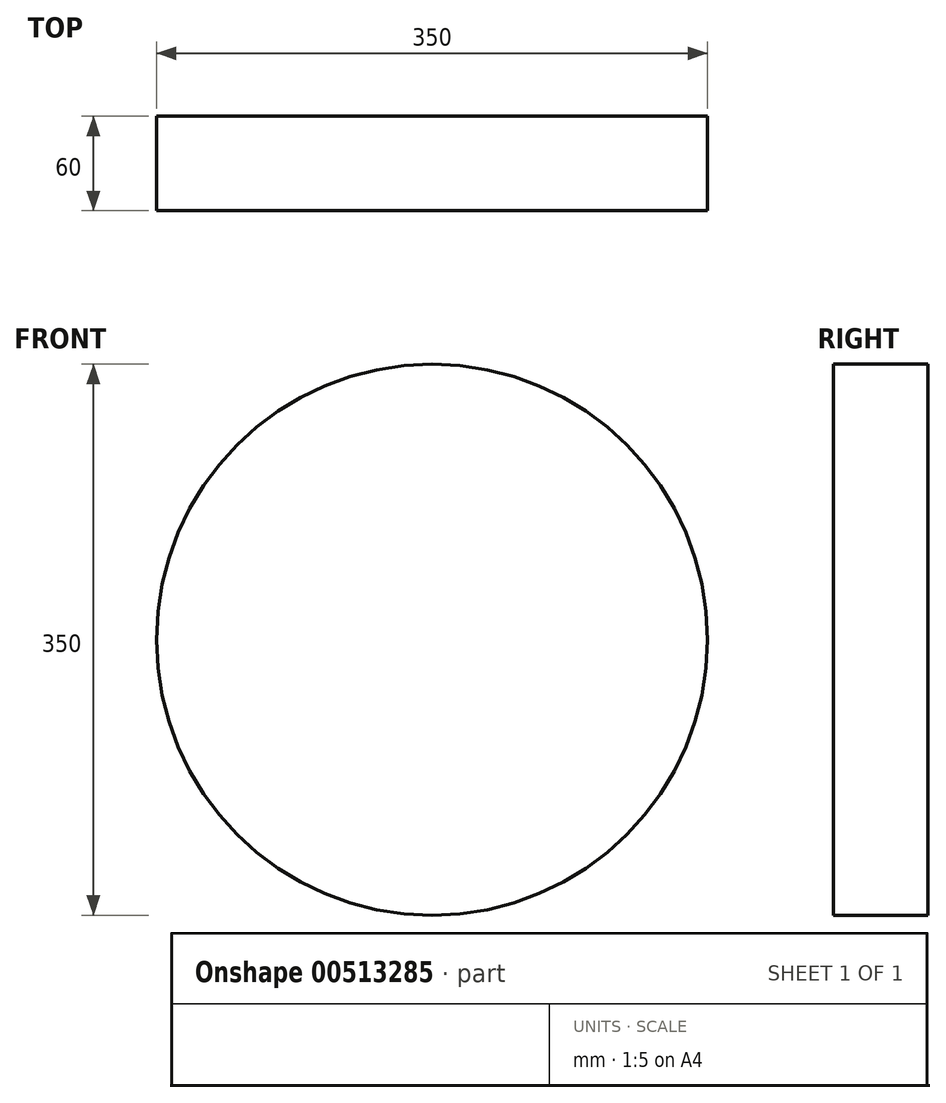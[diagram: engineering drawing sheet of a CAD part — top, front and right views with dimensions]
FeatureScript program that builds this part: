
annotation { "Feature Type Name" : "Feature", "Feature Type Description" : "" }
export const myFeature = defineFeature(function(context is Context, id is Id, definition is map)
    precondition{}
    {
        {
            var Q0;
            Q0=qCreatedBy(makeId("Front.planeOp"),FACE);
            var sketch = newSketch(context, id + "F0", { "sketchPlane" : qUnion([Q0])});
            skCircle(sketch, "E0", {"center": v(0, 0) * mm, "radius": 175 * mm});
            skSolve(sketch);
        }
        {
            var Q0;
            Q0=makeQuery(id+"F0.imprint","IMPRINT",FACE,{"disambiguationData":[TD([[makeQuery(id+"F0.imprint","IMPRINT",EDGE,{"derivedFrom":sQuery(id+"F0.wireOp",EDGE,"E0")}),1.0]])]});
            extrude(context, id + "F1", {"entities" : qUnion([Q0]), "depth" : 60 * mm});
        }
    });
